# Revit family: Mount-Display-Chief-LVS
name_source: partatom
category: Specialty Equipment
revit_build: Autodesk Revit MEP 2012 (Build: 20110916_2132(x64)
units: mm (PartAtom-declared; Revit-internal decimal feet)

## types (4) — shared parameters
Certification = UL Listed
Date Modified = November 19, 2014
Default Elevation = 48 "
Equipment Abbreviation = DM
Family Version = 1.0
Manufacturer = Milestone AV Technologies | Chief Manufacturing
Maximum Extension = 7.4 "
Minimum Depth = 4 "
Model Disclaimer = For more information, contact Milestone AV Technologies | Chief Manufacturing
Product Documentation Link = http://downloads.chiefmfg.com
Product Material = Powder Coat - Chief - Black
Product Page URL = http://www.chiefmfg.com
Solution Type = Universal
URL = http://www.chiefmfg.com
Weight Capacity = 150.000 lb
zz Length 15 = 4 "
zz Length 4 = 7.4 "

## per-type parameters (varying)
| type | Acceptable Flat Panel Sizes | Depth | Description | Height | Model | Mounting Pattern Compatibility | Weight | Width | zz Integer 1 | zz Integer 2 |
| Landscape | Most 42 In. - 80 In. Flat Panels | 4 " | Chief ConnexSys™ Video Wall Landscape Mounting System without Rails | 21.8 " | LVSXU | 760mm x 505mm | 37.000 lb | 35.5 " | 0 | 1 |
| Portrait | Most 40 In. - 80 In. Flat Panels | 4.1 " | Chief ConnexSys™ Video Wall Portrait Mounting System without Rails | 32.5 " | LVSXUP | 800mm x 400mm | 38.000 lb | 19.5 " | 0 | 2 |
| Portrait, With Rails | Most 40 In. - 80 In. Flat Panels | 4.1 " | Chief ConnexSys™ Video Wall Portrait Mounting System with Rails | 32.5 " | LVS1UP | 800mm x 400mm | 42.000 lb | 19.5 " | 1 | 2 |
| Landscape, With Rails | Most 42 In. - 80 In. Flat Panels | 4 " | Chief ConnexSys™ Video Wall Landscape Mounting System with Rails | 21.8 " | LVS1U | 760mm x 505mm | 44.000 lb | 35.5 " | 1 | 1 |

## geometry (parser evidence)
native form markers: Sweep x1
no freeform markers — native parametric forms only
